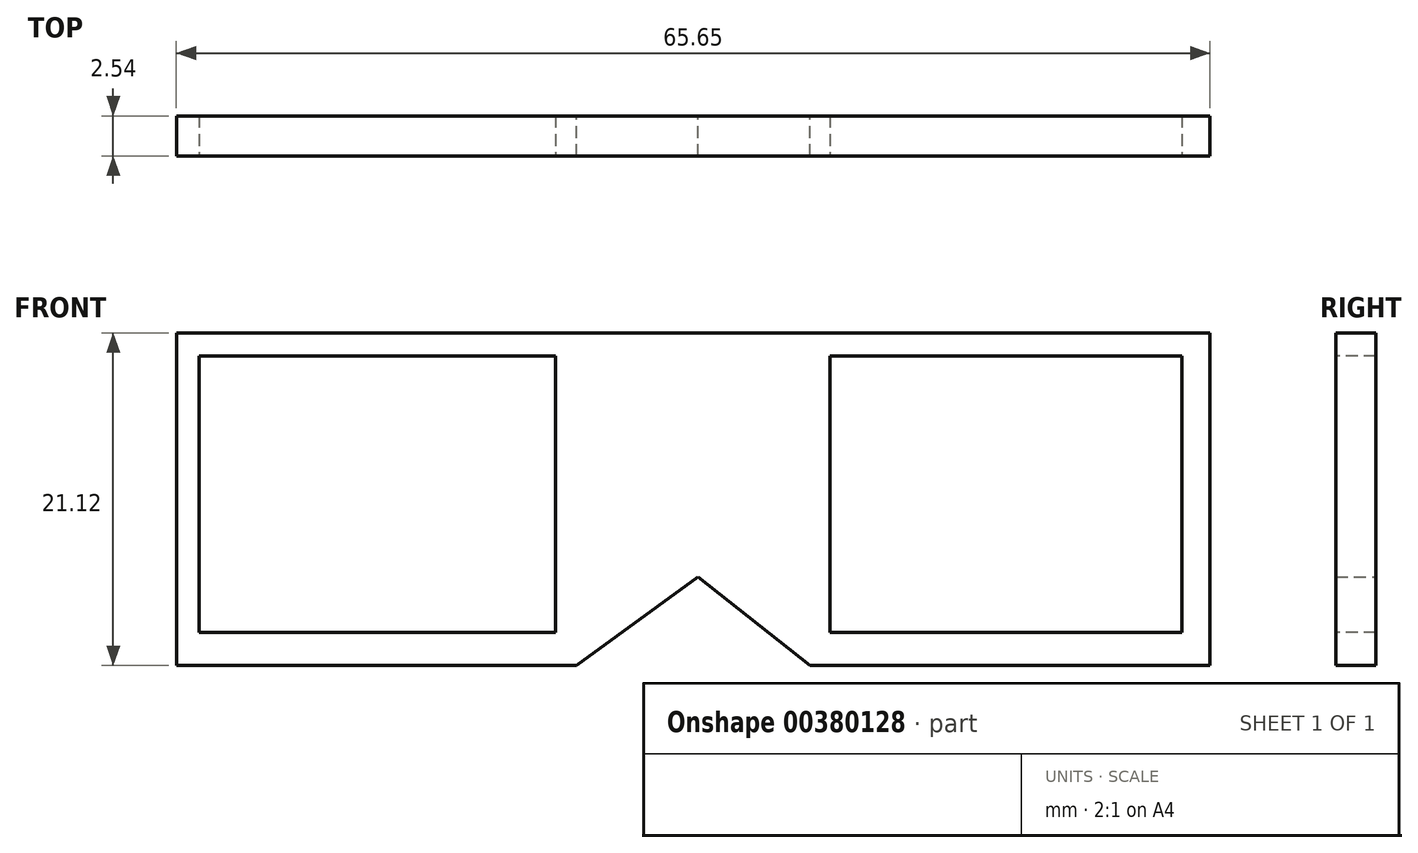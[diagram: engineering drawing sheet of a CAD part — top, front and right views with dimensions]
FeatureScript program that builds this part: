
annotation { "Feature Type Name" : "Feature", "Feature Type Description" : "" }
export const myFeature = defineFeature(function(context is Context, id is Id, definition is map)
    precondition{}
    {
        {
            var Q0;
            Q0=qCreatedBy(makeId("Front.planeOp"),FACE);
            var sketch = newSketch(context, id + "F0", { "sketchPlane" : qUnion([Q0])});
            skLineSegment(sketch, "E0", {"start": v(-29.75, 0) * mm, "end": v(-29.75, 21.12) * mm});
            skLineSegment(sketch, "E1", {"start": v(-29.75, 21.12) * mm, "end": v(-4.35, 21.12) * mm});
            skLineSegment(sketch, "E2", {"start": v(-4.35, 21.12) * mm, "end": v(-4.35, 0) * mm});
            skLineSegment(sketch, "E3", {"start": v(-4.35, 0) * mm, "end": v(-29.75, 0) * mm});
            skLineSegment(sketch, "E4", {"start": v(10.5, 21.12) * mm, "end": v(35.9, 21.12) * mm});
            skLineSegment(sketch, "E5", {"start": v(35.9, 21.12) * mm, "end": v(35.9, 0) * mm});
            skLineSegment(sketch, "E6", {"start": v(35.9, 0) * mm, "end": v(10.5, 0) * mm});
            skLineSegment(sketch, "E7", {"start": v(10.5, 0) * mm, "end": v(10.5, 21.12) * mm});
            skLineSegment(sketch, "E8", {"start": v(-4.35, 0) * mm, "end": v(3.4, 5.63) * mm});
            skLineSegment(sketch, "E9", {"start": v(3.4, 5.63) * mm, "end": v(10.5, 0) * mm});
            skLineSegment(sketch, "E10", {"start": v(-4.35, 3.65) * mm, "end": v(3.4, 8.17) * mm});
            skLineSegment(sketch, "E11", {"start": v(3.4, 8.17) * mm, "end": v(10.5, 3.58) * mm});
            skLineSegment(sketch, "E12", {"start": v(-4.35, 21.12) * mm, "end": v(10.5, 21.12) * mm});
            skSolve(sketch);
        }
        {
            var Q0;
            Q0 = qSketchRegion(id + "F0", true);
            extrude(context, id + "F1", {"entities" : qUnion([Q0]), "depth" : 2.54 * mm});
        }
        {
            var Q0;
            Q0=makeQuery(id+"F1.opExtrude","CAP_FACE",FACE,{"disambiguationData":[OSD([sQuery(id+"F0.wireOp",EDGE,"E0"),sQuery(id+"F0.wireOp",EDGE,"E1"),sQuery(id+"F0.wireOp",EDGE,"E2"),sQuery(id+"F0.wireOp",EDGE,"E3"),sQuery(id+"F0.wireOp",EDGE,"E4"),sQuery(id+"F0.wireOp",EDGE,"E5"),sQuery(id+"F0.wireOp",EDGE,"E6"),sQuery(id+"F0.wireOp",EDGE,"E7"),sQuery(id+"F0.wireOp",EDGE,"E8"),sQuery(id+"F0.wireOp",EDGE,"E9"),sQuery(id+"F0.wireOp",EDGE,"E10"),sQuery(id+"F0.wireOp",EDGE,"E11")])],"isStart":false});
            var sketch = newSketch(context, id + "F2", { "sketchPlane" : qUnion([Q0])});
            skLineSegment(sketch, "E13", {"start": v(-28.31, 2.1) * mm, "end": v(-28.31, 19.67) * mm});
            skLineSegment(sketch, "E14", {"start": v(-28.31, 19.67) * mm, "end": v(-5.67, 19.67) * mm});
            skLineSegment(sketch, "E15", {"start": v(-5.67, 19.67) * mm, "end": v(-5.67, 2.1) * mm});
            skLineSegment(sketch, "E16", {"start": v(-5.67, 2.1) * mm, "end": v(-28.31, 2.1) * mm});
            skLineSegment(sketch, "E17", {"start": v(11.77, 19.67) * mm, "end": v(11.77, 2.1) * mm});
            skLineSegment(sketch, "E18", {"start": v(11.77, 2.1) * mm, "end": v(34.12, 2.1) * mm});
            skLineSegment(sketch, "E19", {"start": v(34.12, 2.1) * mm, "end": v(34.12, 19.67) * mm});
            skLineSegment(sketch, "E20", {"start": v(34.12, 19.67) * mm, "end": v(11.77, 19.67) * mm});
            skSolve(sketch);
        }
        {
            var Q0;
            Q0=makeQuery(id+"F2.imprint","IMPRINT",FACE,{"disambiguationData":[TD([[makeQuery(id+"F2.imprint","IMPRINT",EDGE,{"derivedFrom":sQuery(id+"F2.wireOp",EDGE,"E13")}),-1.0]])]});
            var Q1;
            Q1=makeQuery(id+"F2.imprint","IMPRINT",FACE,{"disambiguationData":[TD([[makeQuery(id+"F2.imprint","IMPRINT",EDGE,{"derivedFrom":sQuery(id+"F2.wireOp",EDGE,"E17")}),1.0]])]});
            extrude(context, id + "F3", {"entities" : qUnion([Q0, Q1]), "oppositeDirection" : true, "depth" : 2.54 * mm});
        }
    });
